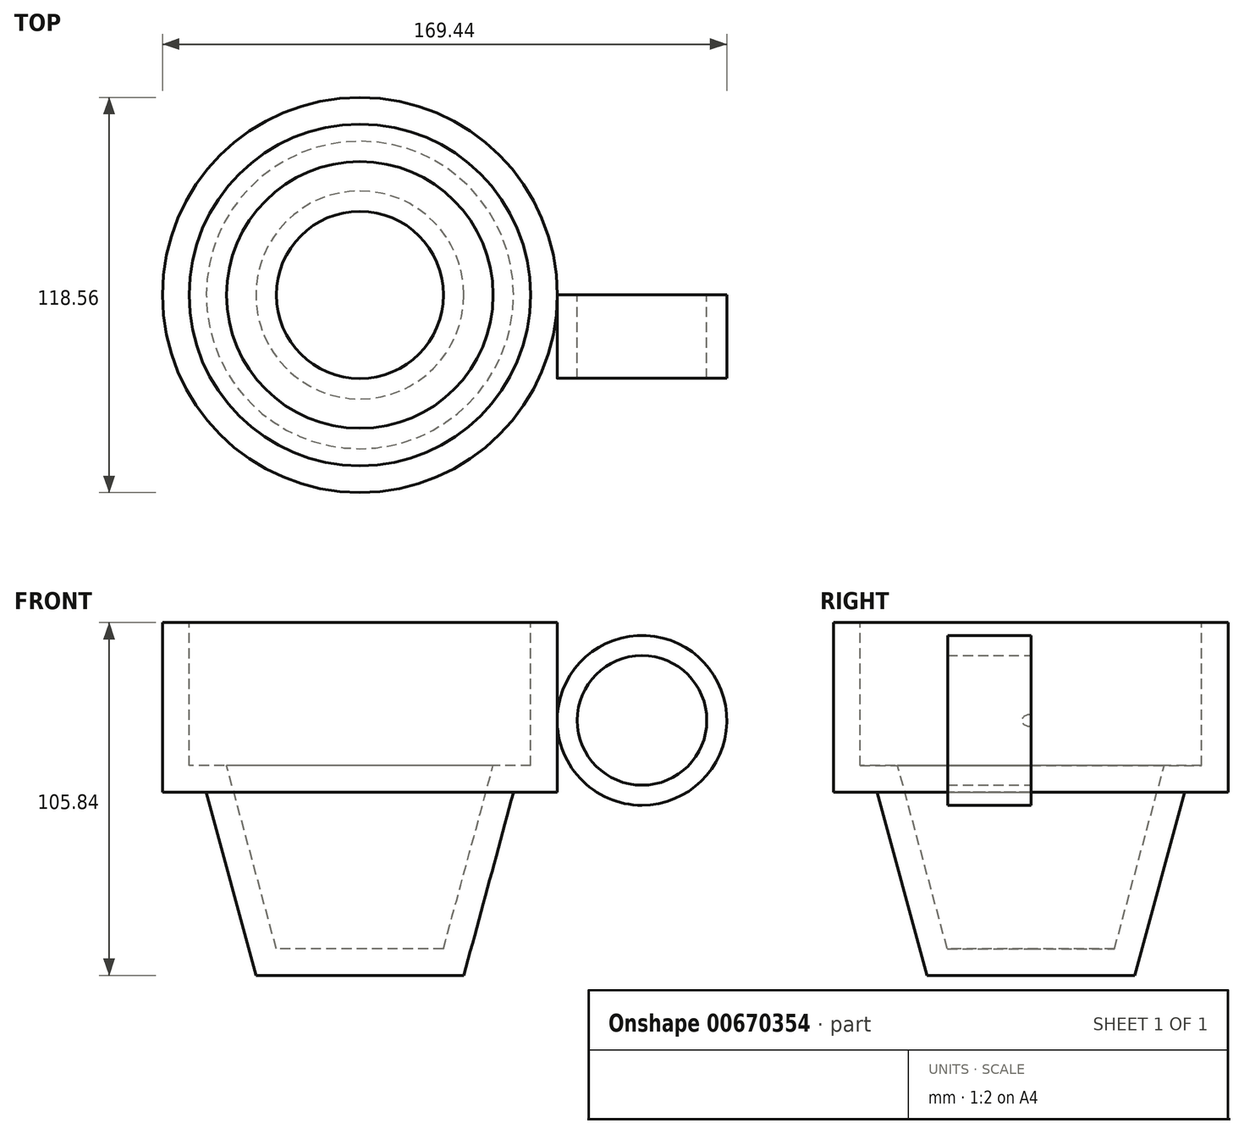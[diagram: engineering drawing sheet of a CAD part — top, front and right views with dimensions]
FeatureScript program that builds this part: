
annotation { "Feature Type Name" : "Feature", "Feature Type Description" : "" }
export const myFeature = defineFeature(function(context is Context, id is Id, definition is map)
    precondition{}
    {
        {
            var Q0;
            Q0=qCreatedBy(makeId("Front.planeOp"),FACE);
            var sketch = newSketch(context, id + "F0", { "sketchPlane" : qUnion([Q0])});
            skLineSegment(sketch, "E0", {"start": v(0, -41.1) * mm, "end": v(25.1, -41.1) * mm});
            skLineSegment(sketch, "E1", {"start": v(25.1, -41.1) * mm, "end": v(40.01, 13.82) * mm});
            skLineSegment(sketch, "E2", {"start": v(40.01, 13.82) * mm, "end": v(51.29, 13.82) * mm});
            skLineSegment(sketch, "E3", {"start": v(51.29, 13.82) * mm, "end": v(51.29, 56.74) * mm});
            skLineSegment(sketch, "E4.0", {"start": v(59.28, 5.83) * mm, "end": v(59.28, 56.74) * mm});
            skLineSegment(sketch, "E4.1", {"start": v(46.12, 5.83) * mm, "end": v(59.28, 5.83) * mm});
            skLineSegment(sketch, "E4.2", {"start": v(31.21, -49.1) * mm, "end": v(46.12, 5.83) * mm});
            skLineSegment(sketch, "E4.3", {"start": v(0, -49.1) * mm, "end": v(31.21, -49.1) * mm});
            skLineSegment(sketch, "E5", {"start": v(51.29, 56.74) * mm, "end": v(59.28, 56.74) * mm});
            skLineSegment(sketch, "E6", {"start": v(0, -41.1) * mm, "end": v(0, -49.1) * mm});
            skSolve(sketch);
        }
        {
            var Q0;
            Q0=makeQuery(id+"F0.imprint","IMPRINT",FACE,{"disambiguationData":[TD([[makeQuery(id+"F0.imprint","IMPRINT",EDGE,{"derivedFrom":sQuery(id+"F0.wireOp",EDGE,"E0")}),-1.0]])]});
            var Q1;
            Q1=sQuery(id+"F0.wireOp",EDGE,"E6");
            revolve(context, id + "F1", {"entities" : qUnion([Q0]), "axis" : qUnion([Q1]), "revolveType" : RevolveType.FULL});
        }
        {
            var Q0;
            Q0=qCreatedBy(makeId("Front.planeOp"),FACE);
            var sketch = newSketch(context, id + "F2", { "sketchPlane" : qUnion([Q0])});
            skCircle(sketch, "E7", {"center": v(84.69, 27.4) * mm, "radius": 25.47 * mm});
            skCircle(sketch, "E8", {"center": v(84.69, 27.4) * mm, "radius": 19.45 * mm});
            skSolve(sketch);
        }
        {
            var Q0;
            Q0=makeQuery(id+"F2.imprint","IMPRINT",FACE,{"disambiguationData":[TD([[makeQuery(id+"F2.imprint","IMPRINT",EDGE,{"derivedFrom":sQuery(id+"F2.wireOp",EDGE,"E7")}),1.0]])]});
            extrude(context, id + "F3", {"entities" : qUnion([Q0]), "operationType" : NewBodyOperationType.ADD, "depth" : 25 * mm, "offsetDistance" : 25 * mm});
        }
    });
